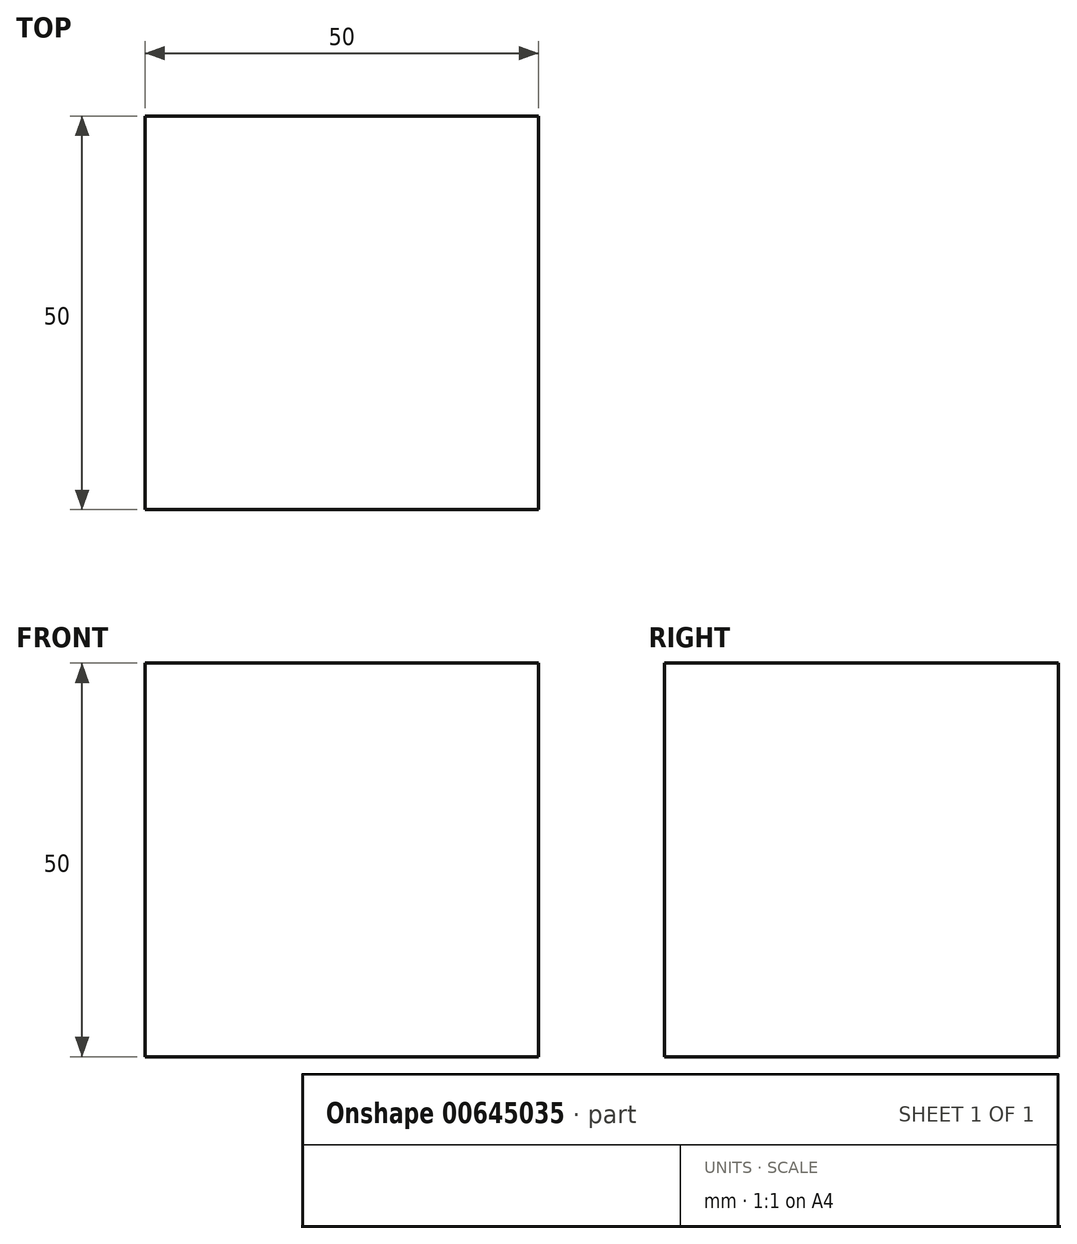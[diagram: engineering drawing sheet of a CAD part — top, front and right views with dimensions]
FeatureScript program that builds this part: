
annotation { "Feature Type Name" : "Feature", "Feature Type Description" : "" }
export const myFeature = defineFeature(function(context is Context, id is Id, definition is map)
    precondition{}
    {
        {
            var Q0;
            Q0=qCreatedBy(makeId("Top.planeOp"),FACE);
            var sketch = newSketch(context, id + "F0", { "sketchPlane" : qUnion([Q0])});
            skLineSegment(sketch, "E0.bottom", {"start": v(25, -25) * mm, "end": v(-25, -25) * mm});
            skLineSegment(sketch, "E0.top", {"start": v(25, 25) * mm, "end": v(-25, 25) * mm});
            skLineSegment(sketch, "E0.left", {"start": v(25, -25) * mm, "end": v(25, 25) * mm});
            skLineSegment(sketch, "E0.right", {"start": v(-25, -25) * mm, "end": v(-25, 25) * mm});
            skPoint(sketch, "E0.middle", {"position": v(0, 0) * mm});
            skSolve(sketch);
        }
        {
            var Q0;
            Q0 = qSketchRegion(id + "F0", true);
            extrude(context, id + "F1", {"entities" : qUnion([Q0]), "depth" : 50 * mm, "offsetDistance" : 25 * mm});
        }
        {
            var Q0;
            Q0=makeQuery(id+"F1.opExtrude","CAP_FACE",FACE,{"disambiguationData":[OSD([sQuery(id+"F0.wireOp",EDGE,"E0.bottom"),sQuery(id+"F0.wireOp",EDGE,"E0.top"),sQuery(id+"F0.wireOp",EDGE,"E0.left"),sQuery(id+"F0.wireOp",EDGE,"E0.right")])],"isStart":false});
            var sketch = newSketch(context, id + "F2", { "sketchPlane" : qUnion([Q0])});
            skCircle(sketch, "E1", {"center": v(0, 0) * mm, "radius": 15 * mm});
            skSolve(sketch);
        }
        {
            var Q0;
            Q0=sQuery(id+"F2.wireOp",EDGE,"E1");
            extrude(context, id + "F3", {"bodyType" : ToolBodyType.SURFACE, "surfaceEntities" : qUnion([Q0]), "depth" : 50 * mm, "offsetDistance" : 25 * mm});
        }
    });
